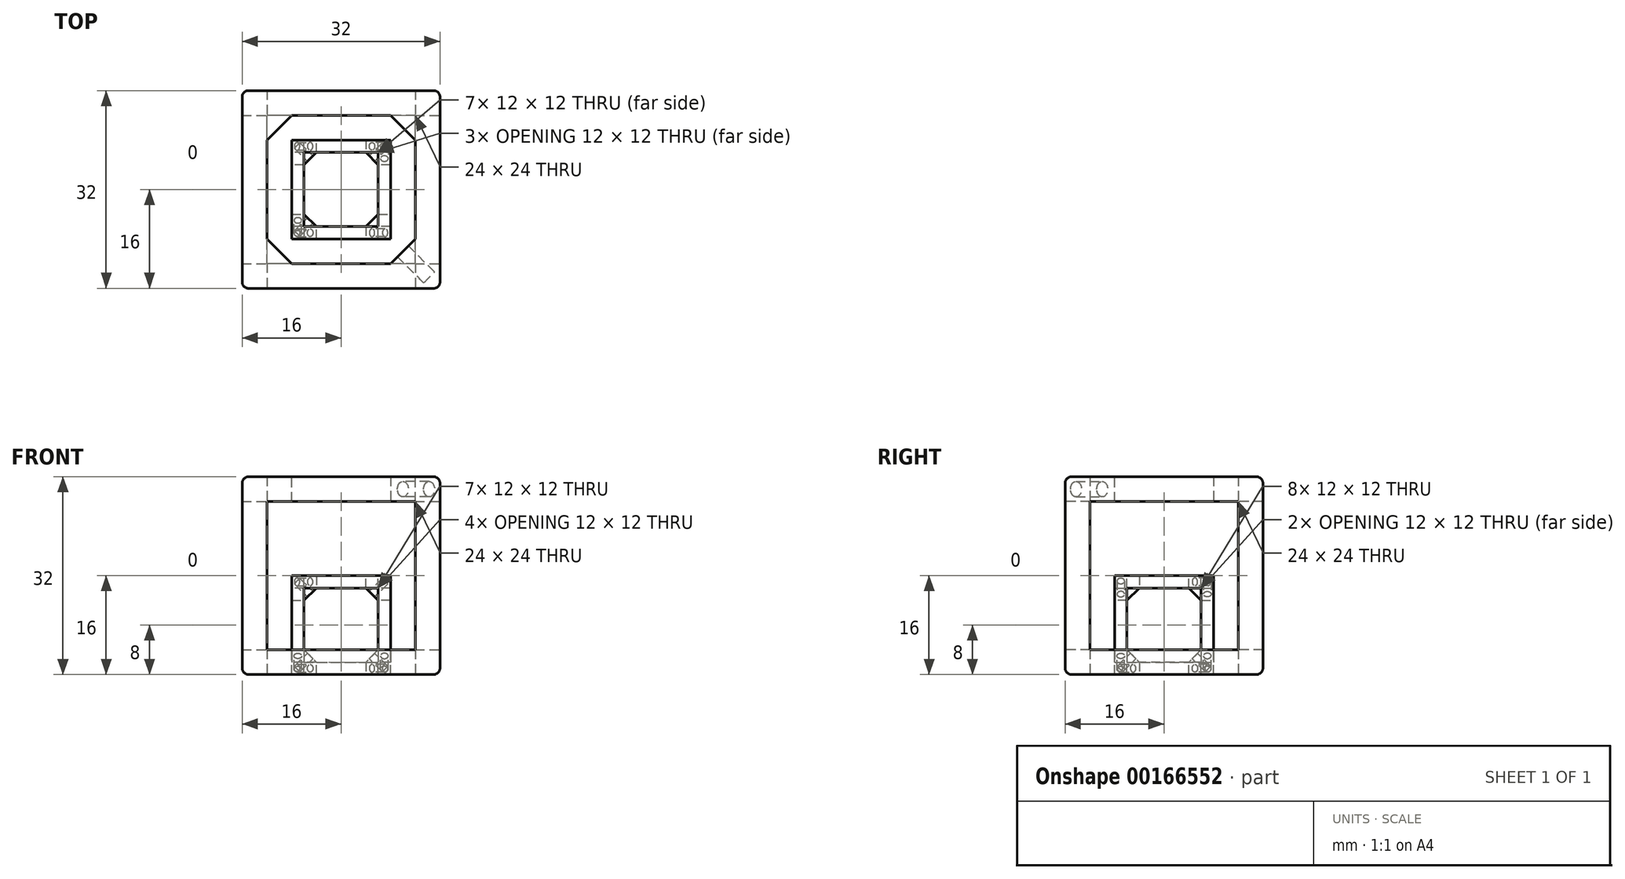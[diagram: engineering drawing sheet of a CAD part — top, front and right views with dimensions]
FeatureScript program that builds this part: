
annotation { "Feature Type Name" : "Feature", "Feature Type Description" : "" }
export const myFeature = defineFeature(function(context is Context, id is Id, definition is map)
    precondition{}
    {
        {
            var Q0;
            Q0=qCreatedBy(makeId("Top.planeOp"),FACE);
            var sketch = newSketch(context, id + "F0", { "sketchPlane" : qUnion([Q0])});
            skLineSegment(sketch, "E0.bottom", {"start": v(8, -8) * mm, "end": v(-8, -8) * mm});
            skLineSegment(sketch, "E0.top", {"start": v(8, 8) * mm, "end": v(-8, 8) * mm});
            skLineSegment(sketch, "E0.left", {"start": v(8, -8) * mm, "end": v(8, 8) * mm});
            skLineSegment(sketch, "E0.right", {"start": v(-8, -8) * mm, "end": v(-8, 8) * mm});
            skPoint(sketch, "E0.middle", {"position": v(0, 0) * mm});
            skLineSegment(sketch, "E1.0", {"start": v(6, -6) * mm, "end": v(-6, -6) * mm});
            skLineSegment(sketch, "E1.1", {"start": v(6, -6) * mm, "end": v(6, 6) * mm});
            skLineSegment(sketch, "E1.2", {"start": v(6, 6) * mm, "end": v(-6, 6) * mm});
            skLineSegment(sketch, "E1.3", {"start": v(-6, -6) * mm, "end": v(-6, 6) * mm});
            skSolve(sketch);
        }
        {
            var Q0;
            Q0=makeQuery(id+"F0.imprint","IMPRINT",FACE,{"disambiguationData":[TD([[makeQuery(id+"F0.imprint","IMPRINT",EDGE,{"derivedFrom":sQuery(id+"F0.wireOp",EDGE,"E0.bottom")}),-1.0]])]});
            extrude(context, id + "F1", {"entities" : qUnion([Q0]), "depth" : 16 * mm});
        }
        {
            var Q0;
            Q0=makeQuery(id+"F1.opExtrude","CAP_FACE",FACE,{"disambiguationData":[OSD([sQuery(id+"F0.wireOp",EDGE,"E0.bottom"),sQuery(id+"F0.wireOp",EDGE,"E0.top"),sQuery(id+"F0.wireOp",EDGE,"E0.left"),sQuery(id+"F0.wireOp",EDGE,"E0.right"),sQuery(id+"F0.wireOp",EDGE,"E1.0"),sQuery(id+"F0.wireOp",EDGE,"E1.1"),sQuery(id+"F0.wireOp",EDGE,"E1.2"),sQuery(id+"F0.wireOp",EDGE,"E1.3")])],"isStart":false});
            var Q1;
            Q1=qCreatedBy(makeId("Top.planeOp"),FACE);
            cPlane(context, id + "F2", {"entities" : qUnion([Q0, Q1]), "cplaneType" : CPlaneType.MID_PLANE, "offset" : 25 * mm, "width" : 150 * mm, "height" : 150 * mm});
        }
        {
            var Q0;
            Q0=qCreatedBy(makeId("Front.planeOp"),FACE);
            var sketch = newSketch(context, id + "F3", { "sketchPlane" : qUnion([Q0])});
            skLineSegment(sketch, "E2", {"start": v(0, 0) * mm, "end": v(0, 21.82) * mm, "construction": true});
            skSolve(sketch);
        }
        {
            var Q0;
            Q0=qCreatedBy(id+"F2.planeOp",FACE);
            var sketch = newSketch(context, id + "F4", { "sketchPlane" : qUnion([Q0])});
            skLineSegment(sketch, "E3", {"start": v(0, 0) * mm, "end": v(13.74, 0) * mm, "construction": true});
            skLineSegment(sketch, "E4", {"start": v(0, 0) * mm, "end": v(0, 14.4) * mm, "construction": true});
            skSolve(sketch);
        }
        {
            var Q0;
            Q0=makeQuery(id+"F1.opExtrude","SWEPT_BODY",BODY,{"disambiguationData":[OSD([sQuery(id+"F0.wireOp",EDGE,"E0.bottom"),sQuery(id+"F0.wireOp",EDGE,"E0.top"),sQuery(id+"F0.wireOp",EDGE,"E0.left"),sQuery(id+"F0.wireOp",EDGE,"E0.right"),sQuery(id+"F0.wireOp",EDGE,"E1.0"),sQuery(id+"F0.wireOp",EDGE,"E1.1"),sQuery(id+"F0.wireOp",EDGE,"E1.2"),sQuery(id+"F0.wireOp",EDGE,"E1.3")])]});
            var Q1;
            Q1=sQuery(id+"F4.wireOp",EDGE,"E3");
            transform(context, id + "F5", {"entities" : qUnion([Q0]), "transformType" : TransformType.ROTATION, "transformAxis" : qUnion([Q1]), "angle" : 90 * degree, "makeCopy" : true});
        }
        {
            var Q0;
            Q0=makeQuery(id+"F5.opPattern","COPY",BODY,{"derivedFrom":makeQuery(id+"F1.opExtrude","SWEPT_BODY",BODY,{"disambiguationData":[OSD([sQuery(id+"F0.wireOp",EDGE,"E0.bottom"),sQuery(id+"F0.wireOp",EDGE,"E0.top"),sQuery(id+"F0.wireOp",EDGE,"E0.left"),sQuery(id+"F0.wireOp",EDGE,"E0.right"),sQuery(id+"F0.wireOp",EDGE,"E1.0"),sQuery(id+"F0.wireOp",EDGE,"E1.1"),sQuery(id+"F0.wireOp",EDGE,"E1.2"),sQuery(id+"F0.wireOp",EDGE,"E1.3")])]}),"instanceName":"1"});
            var Q1;
            Q1=sQuery(id+"F3.wireOp",EDGE,"E2");
            transform(context, id + "F6", {"entities" : qUnion([Q0]), "transformType" : TransformType.ROTATION, "transformAxis" : qUnion([Q1]), "angle" : 90 * degree, "makeCopy" : true});
        }
        {
            var Q0;
            Q0=makeQuery(id+"F1.opExtrude","SWEPT_BODY",BODY,{"disambiguationData":[OSD([sQuery(id+"F0.wireOp",EDGE,"E0.bottom"),sQuery(id+"F0.wireOp",EDGE,"E0.top"),sQuery(id+"F0.wireOp",EDGE,"E0.left"),sQuery(id+"F0.wireOp",EDGE,"E0.right"),sQuery(id+"F0.wireOp",EDGE,"E1.0"),sQuery(id+"F0.wireOp",EDGE,"E1.1"),sQuery(id+"F0.wireOp",EDGE,"E1.2"),sQuery(id+"F0.wireOp",EDGE,"E1.3")])]});
            var Q1;
            Q1=makeQuery(id+"F5.opPattern","COPY",BODY,{"derivedFrom":makeQuery(id+"F1.opExtrude","SWEPT_BODY",BODY,{"disambiguationData":[OSD([sQuery(id+"F0.wireOp",EDGE,"E0.bottom"),sQuery(id+"F0.wireOp",EDGE,"E0.top"),sQuery(id+"F0.wireOp",EDGE,"E0.left"),sQuery(id+"F0.wireOp",EDGE,"E0.right"),sQuery(id+"F0.wireOp",EDGE,"E1.0"),sQuery(id+"F0.wireOp",EDGE,"E1.1"),sQuery(id+"F0.wireOp",EDGE,"E1.2"),sQuery(id+"F0.wireOp",EDGE,"E1.3")])]}),"instanceName":"1"});
            var Q2;
            Q2=makeQuery(id+"F6.opPattern","COPY",BODY,{"derivedFrom":makeQuery(id+"F5.opPattern","COPY",BODY,{"derivedFrom":makeQuery(id+"F1.opExtrude","SWEPT_BODY",BODY,{"disambiguationData":[OSD([sQuery(id+"F0.wireOp",EDGE,"E0.bottom"),sQuery(id+"F0.wireOp",EDGE,"E0.top"),sQuery(id+"F0.wireOp",EDGE,"E0.left"),sQuery(id+"F0.wireOp",EDGE,"E0.right"),sQuery(id+"F0.wireOp",EDGE,"E1.0"),sQuery(id+"F0.wireOp",EDGE,"E1.1"),sQuery(id+"F0.wireOp",EDGE,"E1.2"),sQuery(id+"F0.wireOp",EDGE,"E1.3")])]}),"instanceName":"1"}),"instanceName":"1"});
            booleanBodies(context, id + "F7", {"operationType" : BooleanOperationType.INTERSECTION, "tools" : qUnion([Q0, Q1, Q2])});
        }
        {
            var Q0;
            {var subQ0=sQuery(id+"F0.wireOp",EDGE,"E1.0");var subQ2=sQuery(id+"F0.wireOp",EDGE,"E1.1");Q0=makeQuery(id+"F7.opBoolean","SPLIT",EDGE,{"disambiguationData":[TD([makeQuery(id+"F1.opExtrude","SWEPT_FACE",FACE,{"disambiguationData":[OSD([sQuery(id+"F0.wireOp",EDGE,"E0.left")])]})])],"derivedFrom":makeQuery(id+"F6.opPattern","COPY",EDGE,{"derivedFrom":makeQuery(id+"F5.opPattern","COPY",EDGE,{"derivedFrom":makeQuery(id+"F1.opExtrude","SWEPT_EDGE",EDGE,{"disambiguationData":[OSD([subQ0,subQ2])]}),"instanceName":"1"}),"instanceName":"1"})});}
            var Q1;
            {var subQ0=sQuery(id+"F0.wireOp",EDGE,"E1.1");var subQ3=sQuery(id+"F0.wireOp",EDGE,"E1.2");Q1=makeQuery(id+"F7.opBoolean","SPLIT",EDGE,{"disambiguationData":[TD([makeQuery(id+"F1.opExtrude","SWEPT_FACE",FACE,{"disambiguationData":[OSD([sQuery(id+"F0.wireOp",EDGE,"E0.left")])]})])],"derivedFrom":makeQuery(id+"F6.opPattern","COPY",EDGE,{"derivedFrom":makeQuery(id+"F5.opPattern","COPY",EDGE,{"derivedFrom":makeQuery(id+"F1.opExtrude","SWEPT_EDGE",EDGE,{"disambiguationData":[OSD([subQ0,subQ3])]}),"instanceName":"1"}),"instanceName":"1"})});}
            var Q2;
            {var subQ1=sQuery(id+"F0.wireOp",EDGE,"E1.2");var subQ3=sQuery(id+"F0.wireOp",EDGE,"E1.3");Q2=makeQuery(id+"F7.opBoolean","SPLIT",EDGE,{"disambiguationData":[TD([makeQuery(id+"F1.opExtrude","SWEPT_FACE",FACE,{"disambiguationData":[OSD([sQuery(id+"F0.wireOp",EDGE,"E0.left")])]})])],"derivedFrom":makeQuery(id+"F6.opPattern","COPY",EDGE,{"derivedFrom":makeQuery(id+"F5.opPattern","COPY",EDGE,{"derivedFrom":makeQuery(id+"F1.opExtrude","SWEPT_EDGE",EDGE,{"disambiguationData":[OSD([subQ1,subQ3])]}),"instanceName":"1"}),"instanceName":"1"})});}
            var Q3;
            {var subQ0=sQuery(id+"F0.wireOp",EDGE,"E1.0");var subQ4=sQuery(id+"F0.wireOp",EDGE,"E1.3");Q3=makeQuery(id+"F7.opBoolean","SPLIT",EDGE,{"disambiguationData":[TD([makeQuery(id+"F1.opExtrude","SWEPT_FACE",FACE,{"disambiguationData":[OSD([sQuery(id+"F0.wireOp",EDGE,"E0.left")])]})])],"derivedFrom":makeQuery(id+"F6.opPattern","COPY",EDGE,{"derivedFrom":makeQuery(id+"F5.opPattern","COPY",EDGE,{"derivedFrom":makeQuery(id+"F1.opExtrude","SWEPT_EDGE",EDGE,{"disambiguationData":[OSD([subQ0,subQ4])]}),"instanceName":"1"}),"instanceName":"1"})});}
            chamfer(context, id + "F8", {"entities" : qUnion([Q0, Q1, Q2, Q3]), "width" : 2 * mm, "tangentPropagation" : true});
        }
        {
            var Q0;
            Q0=makeQuery(id+"F8.opChamfer","BLEND_FACE",FACE,{"disambiguationData":[OSD([sQuery(id+"F0.wireOp",EDGE,"E1.0"),sQuery(id+"F0.wireOp",EDGE,"E1.1")])]});
            var sketch = newSketch(context, id + "F9", { "sketchPlane" : qUnion([Q0])});
            skLineSegment(sketch, "E5", {"start": v(6, 5.66) * mm, "end": v(8, 5.66) * mm, "construction": true});
            skLineSegment(sketch, "E6", {"start": v(7, 4.24) * mm, "end": v(7, 7.07) * mm, "construction": true});
            skPoint(sketch, "E7", {"position": v(7, 5.66) * mm});
            skCircle(sketch, "E8", {"center": v(7, 5.66) * mm, "radius": 0.62 * mm});
            skSolve(sketch);
        }
        {
            var Q0;
            Q0 = qSketchRegion(id + "F9", true);
            var Q1;
            {var subQ0=makeQuery(id+"F5.opPattern","COPY",FACE,{"derivedFrom":makeQuery(id+"F1.opExtrude","SWEPT_FACE",FACE,{"disambiguationData":[OSD([sQuery(id+"F0.wireOp",EDGE,"E1.0")])]}),"instanceName":"1"});Q1=makeQuery(id+"F7.opBoolean","MERGE",FACE,{"disambiguationData":[OD(0.0)],"derivedFrom":[subQ0,makeQuery(id+"F6.opPattern","COPY",FACE,{"derivedFrom":subQ0,"instanceName":"1"})]});}
            var Q2;
            {var subQ0=sQuery(id+"F0.wireOp",EDGE,"E1.0");var subQ1=makeQuery(id+"F5.opPattern","COPY",FACE,{"derivedFrom":makeQuery(id+"F1.opExtrude","SWEPT_FACE",FACE,{"disambiguationData":[OSD([subQ0])]}),"instanceName":"1"});var subQ6=sQuery(id+"F0.wireOp",EDGE,"E1.2");Q2=makeQuery(id+"F7.opBoolean","SPLIT",FACE,{"disambiguationData":[TD([subQ1])],"derivedFrom":makeQuery(id+"F1.opExtrude","SWEPT_FACE",FACE,{"disambiguationData":[OSD([subQ6])]})});}
            extrude(context, id + "F10", {"entities" : qUnion([Q0]), "operationType" : NewBodyOperationType.REMOVE, "oppositeDirection" : true, "endBoundEntityFace" : qUnion([Q1]), "depth" : 3 * mm});
        }
        {
            var Q0;
            {var subQ0=makeQuery(id+"F1.opExtrude","SWEPT_BODY",BODY,{"disambiguationData":[OSD([sQuery(id+"F0.wireOp",EDGE,"E0.bottom"),sQuery(id+"F0.wireOp",EDGE,"E0.top"),sQuery(id+"F0.wireOp",EDGE,"E0.left"),sQuery(id+"F0.wireOp",EDGE,"E0.right"),sQuery(id+"F0.wireOp",EDGE,"E1.0"),sQuery(id+"F0.wireOp",EDGE,"E1.1"),sQuery(id+"F0.wireOp",EDGE,"E1.2"),sQuery(id+"F0.wireOp",EDGE,"E1.3")])]});var subQ1=makeQuery(id+"F5.opPattern","COPY",BODY,{"derivedFrom":subQ0,"instanceName":"1"});Q0=makeQuery(id+"F7.opBoolean","INTERSECT",BODY,{"derivedFrom":[subQ0,subQ1,makeQuery(id+"F6.opPattern","COPY",BODY,{"derivedFrom":subQ1,"instanceName":"1"})]});}
            var Q1;
            Q1=sQuery(id+"F3.wireOp",EDGE,"E2");
            circularPattern(context, id + "F11", {"entities" : qUnion([Q0]), "axis" : qUnion([Q1]), "angle" : 90 * degree, "instanceCount" : 4});
        }
        {
            var Q0;
            {var subQ0=makeQuery(id+"F1.opExtrude","SWEPT_BODY",BODY,{"disambiguationData":[OSD([sQuery(id+"F0.wireOp",EDGE,"E0.bottom"),sQuery(id+"F0.wireOp",EDGE,"E0.top"),sQuery(id+"F0.wireOp",EDGE,"E0.left"),sQuery(id+"F0.wireOp",EDGE,"E0.right"),sQuery(id+"F0.wireOp",EDGE,"E1.0"),sQuery(id+"F0.wireOp",EDGE,"E1.1"),sQuery(id+"F0.wireOp",EDGE,"E1.2"),sQuery(id+"F0.wireOp",EDGE,"E1.3")])]});var subQ1=makeQuery(id+"F5.opPattern","COPY",BODY,{"derivedFrom":subQ0,"instanceName":"1"});Q0=makeQuery(id+"F11.opPattern","COPY",BODY,{"derivedFrom":makeQuery(id+"F7.opBoolean","INTERSECT",BODY,{"derivedFrom":[subQ0,subQ1,makeQuery(id+"F6.opPattern","COPY",BODY,{"derivedFrom":subQ1,"instanceName":"1"})]}),"instanceName":"3"});}
            var Q1;
            {var subQ0=makeQuery(id+"F1.opExtrude","SWEPT_BODY",BODY,{"disambiguationData":[OSD([sQuery(id+"F0.wireOp",EDGE,"E0.bottom"),sQuery(id+"F0.wireOp",EDGE,"E0.top"),sQuery(id+"F0.wireOp",EDGE,"E0.left"),sQuery(id+"F0.wireOp",EDGE,"E0.right"),sQuery(id+"F0.wireOp",EDGE,"E1.0"),sQuery(id+"F0.wireOp",EDGE,"E1.1"),sQuery(id+"F0.wireOp",EDGE,"E1.2"),sQuery(id+"F0.wireOp",EDGE,"E1.3")])]});var subQ1=makeQuery(id+"F5.opPattern","COPY",BODY,{"derivedFrom":subQ0,"instanceName":"1"});Q1=makeQuery(id+"F11.opPattern","COPY",BODY,{"derivedFrom":makeQuery(id+"F7.opBoolean","INTERSECT",BODY,{"derivedFrom":[subQ0,subQ1,makeQuery(id+"F6.opPattern","COPY",BODY,{"derivedFrom":subQ1,"instanceName":"1"})]}),"instanceName":"1"});}
            var Q2;
            Q2=sQuery(id+"F4.wireOp",EDGE,"E3");
            circularPattern(context, id + "F12", {"entities" : qUnion([Q0, Q1]), "axis" : qUnion([Q2]), "angle" : 90 * degree, "instanceCount" : 4});
        }
        {
            var Q0;
            Q0=makeQuery(id+"F12.opPattern","COPY",EDGE,{"derivedFrom":makeQuery(id+"F11.opPattern","COPY",EDGE,{"derivedFrom":makeQuery(id+"F1.opExtrude","CAP_EDGE",EDGE,{"disambiguationData":[OSD([sQuery(id+"F0.wireOp",EDGE,"E0.right")])],"isStart":true}),"instanceName":"3"}),"instanceName":"3"});
            var Q1;
            Q1=makeQuery(id+"F12.opPattern","COPY",EDGE,{"derivedFrom":makeQuery(id+"F11.opPattern","COPY",EDGE,{"derivedFrom":makeQuery(id+"F1.opExtrude","CAP_EDGE",EDGE,{"disambiguationData":[OSD([sQuery(id+"F0.wireOp",EDGE,"E0.bottom")])],"isStart":true}),"instanceName":"3"}),"instanceName":"3"});
            var Q2;
            Q2=makeQuery(id+"F12.opPattern","COPY",EDGE,{"derivedFrom":makeQuery(id+"F11.opPattern","COPY",EDGE,{"derivedFrom":makeQuery(id+"F1.opExtrude","SWEPT_EDGE",EDGE,{"disambiguationData":[OSD([sQuery(id+"F0.wireOp",EDGE,"E0.bottom"),sQuery(id+"F0.wireOp",EDGE,"E0.right")])]}),"instanceName":"3"}),"instanceName":"3"});
            var Q3;
            Q3=makeQuery(id+"F12.opPattern","COPY",EDGE,{"derivedFrom":makeQuery(id+"F11.opPattern","COPY",EDGE,{"derivedFrom":makeQuery(id+"F1.opExtrude","SWEPT_EDGE",EDGE,{"disambiguationData":[OSD([sQuery(id+"F0.wireOp",EDGE,"E0.top"),sQuery(id+"F0.wireOp",EDGE,"E0.left")])]}),"instanceName":"3"}),"instanceName":"3"});
            var Q4;
            Q4=makeQuery(id+"F12.opPattern","COPY",EDGE,{"derivedFrom":makeQuery(id+"F11.opPattern","COPY",EDGE,{"derivedFrom":makeQuery(id+"F1.opExtrude","CAP_EDGE",EDGE,{"disambiguationData":[OSD([sQuery(id+"F0.wireOp",EDGE,"E0.left")])],"isStart":true}),"instanceName":"3"}),"instanceName":"3"});
            var Q5;
            Q5=makeQuery(id+"F12.opPattern","COPY",EDGE,{"derivedFrom":makeQuery(id+"F11.opPattern","COPY",EDGE,{"derivedFrom":makeQuery(id+"F1.opExtrude","CAP_EDGE",EDGE,{"disambiguationData":[OSD([sQuery(id+"F0.wireOp",EDGE,"E0.top")])],"isStart":true}),"instanceName":"3"}),"instanceName":"3"});
            var Q6;
            Q6=makeQuery(id+"F12.opPattern","COPY",EDGE,{"derivedFrom":makeQuery(id+"F11.opPattern","COPY",EDGE,{"derivedFrom":makeQuery(id+"F1.opExtrude","CAP_EDGE",EDGE,{"disambiguationData":[OSD([sQuery(id+"F0.wireOp",EDGE,"E0.left")])],"isStart":false}),"instanceName":"3"}),"instanceName":"3"});
            var Q7;
            Q7=makeQuery(id+"F12.opPattern","COPY",EDGE,{"derivedFrom":makeQuery(id+"F11.opPattern","COPY",EDGE,{"derivedFrom":makeQuery(id+"F1.opExtrude","CAP_EDGE",EDGE,{"disambiguationData":[OSD([sQuery(id+"F0.wireOp",EDGE,"E0.top")])],"isStart":false}),"instanceName":"3"}),"instanceName":"3"});
            var Q8;
            Q8=makeQuery(id+"F12.opPattern","COPY",EDGE,{"derivedFrom":makeQuery(id+"F11.opPattern","COPY",EDGE,{"derivedFrom":makeQuery(id+"F1.opExtrude","CAP_EDGE",EDGE,{"disambiguationData":[OSD([sQuery(id+"F0.wireOp",EDGE,"E0.bottom")])],"isStart":false}),"instanceName":"3"}),"instanceName":"3"});
            var Q9;
            Q9=makeQuery(id+"F12.opPattern","COPY",EDGE,{"derivedFrom":makeQuery(id+"F11.opPattern","COPY",EDGE,{"derivedFrom":makeQuery(id+"F1.opExtrude","SWEPT_EDGE",EDGE,{"disambiguationData":[OSD([sQuery(id+"F0.wireOp",EDGE,"E0.bottom"),sQuery(id+"F0.wireOp",EDGE,"E0.left")])]}),"instanceName":"3"}),"instanceName":"3"});
            var Q10;
            Q10=makeQuery(id+"F12.opPattern","COPY",EDGE,{"derivedFrom":makeQuery(id+"F11.opPattern","COPY",EDGE,{"derivedFrom":makeQuery(id+"F1.opExtrude","CAP_EDGE",EDGE,{"disambiguationData":[OSD([sQuery(id+"F0.wireOp",EDGE,"E0.right")])],"isStart":false}),"instanceName":"3"}),"instanceName":"3"});
            var Q11;
            Q11=makeQuery(id+"F12.opPattern","COPY",EDGE,{"derivedFrom":makeQuery(id+"F11.opPattern","COPY",EDGE,{"derivedFrom":makeQuery(id+"F1.opExtrude","SWEPT_EDGE",EDGE,{"disambiguationData":[OSD([sQuery(id+"F0.wireOp",EDGE,"E0.top"),sQuery(id+"F0.wireOp",EDGE,"E0.right")])]}),"instanceName":"3"}),"instanceName":"3"});
            fillet(context, id + "F13", {"entities" : qUnion([Q0, Q1, Q2, Q3, Q4, Q5, Q6, Q7, Q8, Q9, Q10, Q11]), "radius" : .5 * mm, "tangentPropagation" : true, "allowEdgeOverflow" : false});
        }
        {
            var Q0;
            {var subQ0=makeQuery(id+"F1.opExtrude","SWEPT_BODY",BODY,{"disambiguationData":[OSD([sQuery(id+"F0.wireOp",EDGE,"E0.bottom"),sQuery(id+"F0.wireOp",EDGE,"E0.top"),sQuery(id+"F0.wireOp",EDGE,"E0.left"),sQuery(id+"F0.wireOp",EDGE,"E0.right"),sQuery(id+"F0.wireOp",EDGE,"E1.0"),sQuery(id+"F0.wireOp",EDGE,"E1.1"),sQuery(id+"F0.wireOp",EDGE,"E1.2"),sQuery(id+"F0.wireOp",EDGE,"E1.3")])]});var subQ1=makeQuery(id+"F5.opPattern","COPY",BODY,{"derivedFrom":subQ0,"instanceName":"1"});Q0=makeQuery(id+"F12.opPattern","COPY",BODY,{"derivedFrom":makeQuery(id+"F11.opPattern","COPY",BODY,{"derivedFrom":makeQuery(id+"F7.opBoolean","INTERSECT",BODY,{"derivedFrom":[subQ0,subQ1,makeQuery(id+"F6.opPattern","COPY",BODY,{"derivedFrom":subQ1,"instanceName":"1"})]}),"instanceName":"3"}),"instanceName":"3"});}
            var Q1;
            Q1=qCreatedBy(makeId("Origin.pointOp"),VERTEX);
            transform(context, id + "F14", {"entities" : qUnion([Q0]), "transformType" : TransformType.SCALE_UNIFORMLY, "scale" : 2, "scalePoint" : qUnion([Q1]), "makeCopy" : false});
        }
    });
